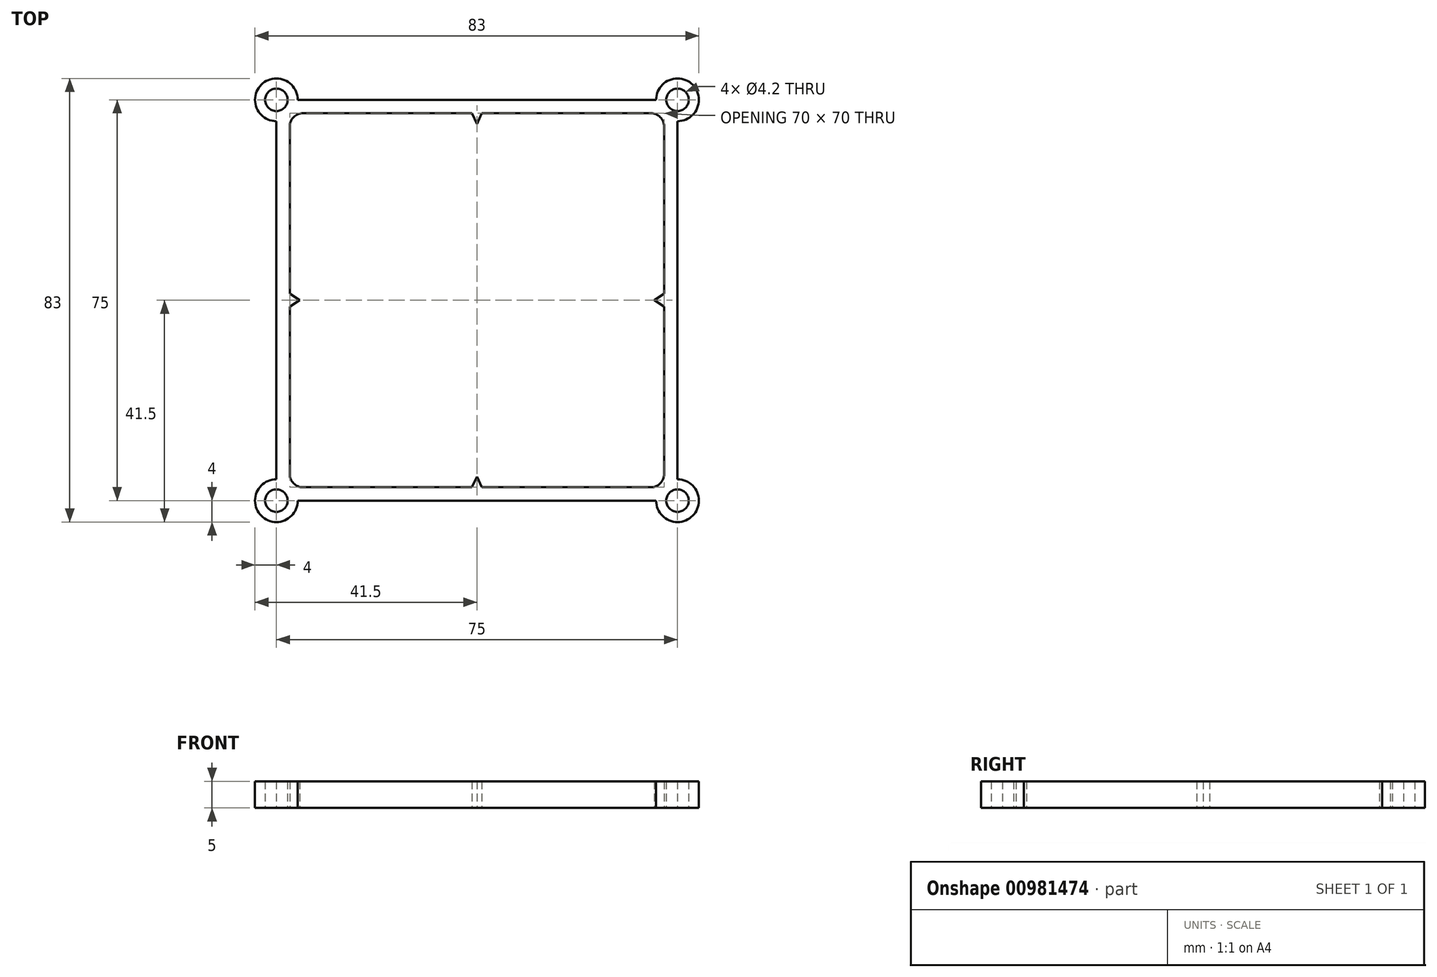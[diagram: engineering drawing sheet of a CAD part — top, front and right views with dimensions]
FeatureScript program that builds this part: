
annotation { "Feature Type Name" : "Feature", "Feature Type Description" : "" }
export const myFeature = defineFeature(function(context is Context, id is Id, definition is map)
    precondition{}
    {
        {
            var Q0;
            Q0=qCreatedBy(makeId("Top.planeOp"),FACE);
            var sketch = newSketch(context, id + "F0", { "sketchPlane" : qUnion([Q0])});
            skLineSegment(sketch, "E0.bottom", {"start": v(33.5, 37.5) * mm, "end": v(-33.5, 37.5) * mm});
            skLineSegment(sketch, "E0.top", {"start": v(33.5, -37.5) * mm, "end": v(-33.5, -37.5) * mm});
            skLineSegment(sketch, "E0.left", {"start": v(37.5, 33.5) * mm, "end": v(37.5, -33.5) * mm});
            skLineSegment(sketch, "E0.right", {"start": v(-37.5, 33.5) * mm, "end": v(-37.5, -33.5) * mm});
            skPoint(sketch, "E0.middle", {"position": v(0, 0) * mm});
            skArc(sketch, "E1", {"start": v(-33.5, 37.5) * mm, "mid": v(-40.33, 40.33) * mm, "end": v(-37.5, 33.5) * mm});
            skArc(sketch, "E2", {"start": v(37.5, 33.5) * mm, "mid": v(40.33, 40.33) * mm, "end": v(33.5, 37.5) * mm});
            skArc(sketch, "E3", {"start": v(33.5, -37.5) * mm, "mid": v(40.33, -40.33) * mm, "end": v(37.5, -33.5) * mm});
            skArc(sketch, "E4", {"start": v(-37.5, -33.5) * mm, "mid": v(-40.33, -40.33) * mm, "end": v(-33.5, -37.5) * mm});
            skCircle(sketch, "E5", {"center": v(-37.5, -37.5) * mm, "radius": 2.1 * mm});
            skCircle(sketch, "E6", {"center": v(37.5, -37.5) * mm, "radius": 2.1 * mm});
            skCircle(sketch, "E7", {"center": v(37.5, 37.5) * mm, "radius": 2.1 * mm});
            skCircle(sketch, "E8", {"center": v(-37.5, 37.5) * mm, "radius": 2.1 * mm});
            skLineSegment(sketch, "E9.bottom", {"start": v(32.5, 35) * mm, "end": v(0.92, 35) * mm});
            skLineSegment(sketch, "E9.top", {"start": v(32.5, -35) * mm, "end": v(0.92, -35) * mm});
            skLineSegment(sketch, "E9.left", {"start": v(35, 32.5) * mm, "end": v(35, 1.2) * mm});
            skLineSegment(sketch, "E9.right", {"start": v(-35, 32.5) * mm, "end": v(-35, 1.2) * mm});
            skPoint(sketch, "E10.visualSharp", {"position": v(35, 35) * mm});
            skArc(sketch, "E10.filletArc", {"start": v(35, 32.5) * mm, "mid": v(34.27, 34.27) * mm, "end": v(32.5, 35) * mm});
            skPoint(sketch, "E11.visualSharp", {"position": v(-35, 35) * mm});
            skArc(sketch, "E11.filletArc", {"start": v(-32.5, 35) * mm, "mid": v(-34.27, 34.27) * mm, "end": v(-35, 32.5) * mm});
            skPoint(sketch, "E12.visualSharp", {"position": v(-35, -35) * mm});
            skArc(sketch, "E12.filletArc", {"start": v(-35, -32.5) * mm, "mid": v(-34.27, -34.27) * mm, "end": v(-32.5, -35) * mm});
            skPoint(sketch, "E13.visualSharp", {"position": v(35, -35) * mm});
            skArc(sketch, "E13.filletArc", {"start": v(32.5, -35) * mm, "mid": v(34.27, -34.27) * mm, "end": v(35, -32.5) * mm});
            skLineSegment(sketch, "E14", {"start": v(0, 33) * mm, "end": v(-0.92, 35) * mm});
            skLineSegment(sketch, "E15.MirrorCS", {"start": v(0, 33) * mm, "end": v(0.92, 35) * mm});
            skPoint(sketch, "E16.start.orphan", {"position": v(0, 35) * mm});
            skLineSegment(sketch, "E17.trimOffspring", {"start": v(-0.92, 35) * mm, "end": v(-32.5, 35) * mm});
            skLineSegment(sketch, "E18", {"start": v(33.16, 0) * mm, "end": v(35, -1.2) * mm});
            skLineSegment(sketch, "E19.MirrorCS", {"start": v(33.16, 0) * mm, "end": v(35, 1.2) * mm});
            skPoint(sketch, "E20.start.orphan", {"position": v(35, 0) * mm});
            skLineSegment(sketch, "E21.trimOffspring", {"start": v(35, -1.2) * mm, "end": v(35, -32.5) * mm});
            skLineSegment(sketch, "E22.MirrorCS", {"start": v(-33.16, 0) * mm, "end": v(-35, 1.2) * mm});
            skLineSegment(sketch, "E23.MirrorCS", {"start": v(-33.16, 0) * mm, "end": v(-35, -1.2) * mm});
            skLineSegment(sketch, "E24.MirrorCS", {"start": v(0, -33) * mm, "end": v(-0.92, -35) * mm});
            skLineSegment(sketch, "E25.MirrorCS", {"start": v(0, -33) * mm, "end": v(0.92, -35) * mm});
            skLineSegment(sketch, "E26.trimOffspring", {"start": v(-0.92, -35) * mm, "end": v(-32.5, -35) * mm});
            skLineSegment(sketch, "E27.trimOffspring", {"start": v(-35, -1.2) * mm, "end": v(-35, -32.5) * mm});
            skPoint(sketch, "E28.start.orphan", {"position": v(9.35, 0) * mm});
            skSolve(sketch);
        }
        {
            var Q0;
            Q0=makeQuery(id+"F0.imprint","IMPRINT",FACE,{"disambiguationData":[TD([[makeQuery(id+"F0.imprint","IMPRINT",EDGE,{"derivedFrom":sQuery(id+"F0.wireOp",EDGE,"E0.bottom")}),1.0]])]});
            extrude(context, id + "F1", {"entities" : qUnion([Q0]), "depth" : 5 * mm, "offsetDistance" : 25 * mm});
        }
    });
